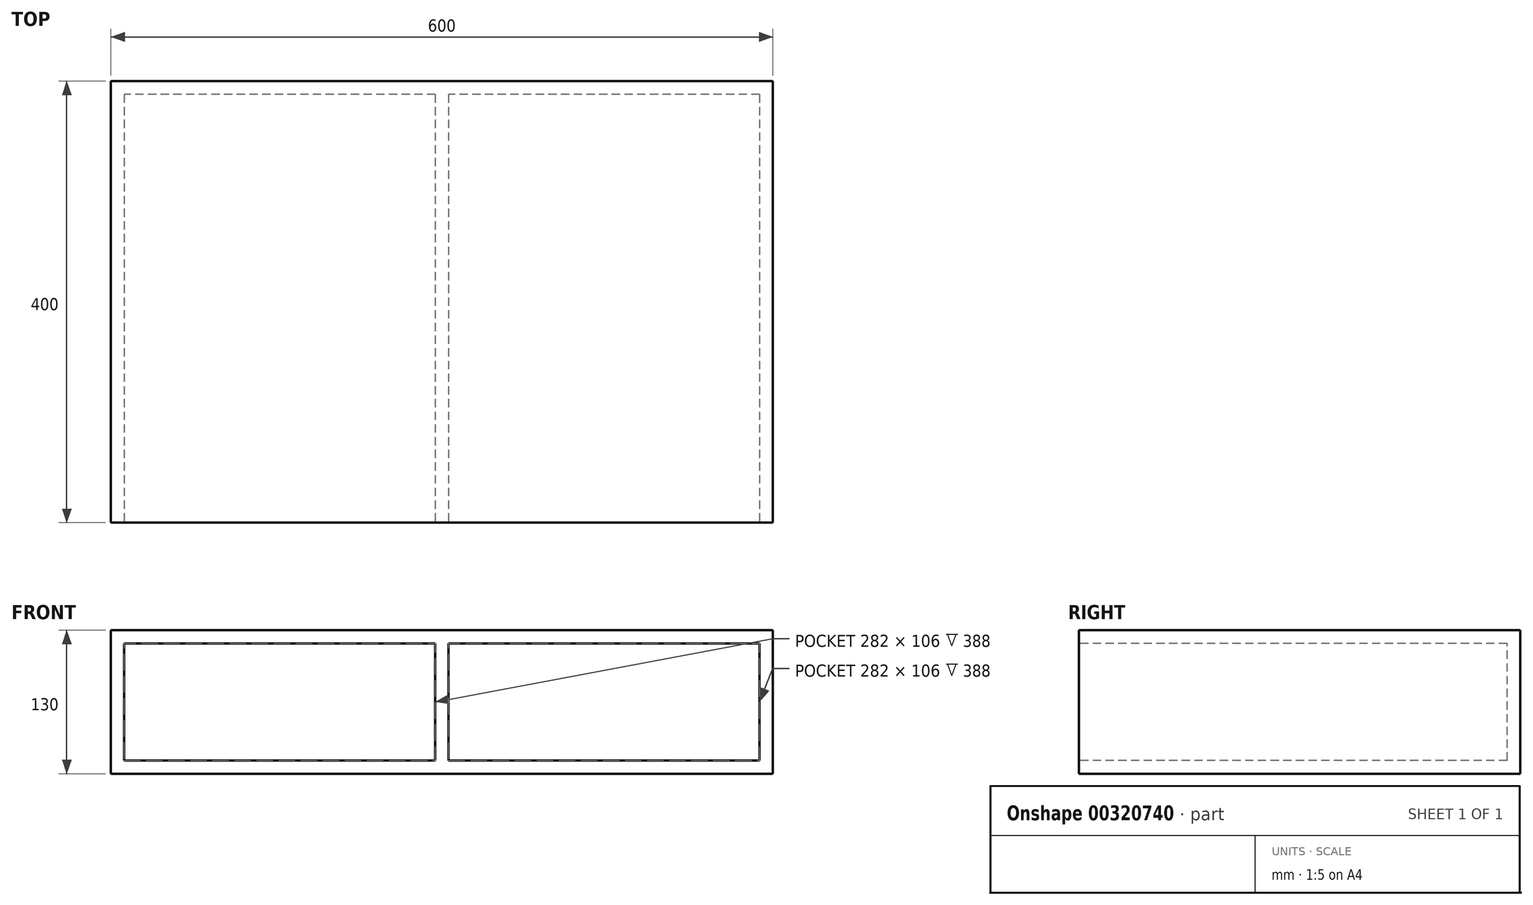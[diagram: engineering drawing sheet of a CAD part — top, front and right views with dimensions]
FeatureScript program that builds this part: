
annotation { "Feature Type Name" : "Feature", "Feature Type Description" : "" }
export const myFeature = defineFeature(function(context is Context, id is Id, definition is map)
    precondition{}
    {
        {
            var Q0;
            Q0=qCreatedBy(makeId("Front.planeOp"),FACE);
            var sketch = newSketch(context, id + "F0", { "sketchPlane" : qUnion([Q0])});
            skLineSegment(sketch, "E0.bottom", {"start": v(300, -65) * mm, "end": v(-300, -65) * mm});
            skLineSegment(sketch, "E0.top", {"start": v(300, 65) * mm, "end": v(-300, 65) * mm});
            skLineSegment(sketch, "E0.left", {"start": v(300, -65) * mm, "end": v(300, 65) * mm});
            skLineSegment(sketch, "E0.right", {"start": v(-300, -65) * mm, "end": v(-300, 65) * mm});
            skPoint(sketch, "E0.middle", {"position": v(0, 0) * mm});
            skSolve(sketch);
        }
        {
            var Q0;
            Q0=makeQuery(id+"F0.imprint","IMPRINT",FACE,{"disambiguationData":[TD([[makeQuery(id+"F0.imprint","IMPRINT",EDGE,{"derivedFrom":sQuery(id+"F0.wireOp",EDGE,"E0.bottom")}),-1.0]])]});
            extrude(context, id + "F1", {"entities" : qUnion([Q0]), "oppositeDirection" : true, "depth" : 400 * mm});
        }
        {
            var Q0;
            Q0=makeQuery(id+"F1.opExtrude","CAP_FACE",FACE,{"disambiguationData":[OSD([sQuery(id+"F0.wireOp",EDGE,"E0.bottom"),sQuery(id+"F0.wireOp",EDGE,"E0.top"),sQuery(id+"F0.wireOp",EDGE,"E0.left"),sQuery(id+"F0.wireOp",EDGE,"E0.right")])],"isStart":true});
            shell(context, id + "F2", {"entities" : qUnion([Q0]), "thickness" : 12 * mm});
        }
        {
            var Q0;
            Q0=makeQuery(id+"F1.opExtrude","CAP_FACE",FACE,{"disambiguationData":[OSD([sQuery(id+"F0.wireOp",EDGE,"E0.bottom"),sQuery(id+"F0.wireOp",EDGE,"E0.top"),sQuery(id+"F0.wireOp",EDGE,"E0.left"),sQuery(id+"F0.wireOp",EDGE,"E0.right")])],"isStart":true});
            var sketch = newSketch(context, id + "F3", { "sketchPlane" : qUnion([Q0])});
            skLineSegment(sketch, "E1.bottom", {"start": v(6, -62.5) * mm, "end": v(-6, -62.5) * mm});
            skLineSegment(sketch, "E1.top", {"start": v(6, 62.5) * mm, "end": v(-6, 62.5) * mm});
            skLineSegment(sketch, "E1.left", {"start": v(6, -62.5) * mm, "end": v(6, 62.5) * mm});
            skLineSegment(sketch, "E1.right", {"start": v(-6, -62.5) * mm, "end": v(-6, 62.5) * mm});
            skPoint(sketch, "E1.middle", {"position": v(0, 0) * mm});
            skSolve(sketch);
        }
        {
            var Q0;
            {var subQ0=sQuery(id+"F3.wireOp",EDGE,"E1.left");var subQ1=sQuery(id+"F0.wireOp",EDGE,"E0.bottom");var subQ2=makeQuery(id+"F2.opShell","OFFSET_EDGE",EDGE,{"disambiguationData":[OSD([subQ1]),TDD([makeQuery(id+"F1.opExtrude","CAP_EDGE",EDGE,{"disambiguationData":[OSD([subQ1])],"isStart":true})])]});var subQ3=makeQuery(id+"F3.imprint","INTERSECT",VERTEX,{"derivedFrom":[subQ2,subQ0]});Q0=makeQuery(id+"F3.imprint","IMPRINT",FACE,{"disambiguationData":[TD([[makeQuery(id+"F3.imprint","IMPRINT",EDGE,{"disambiguationData":[TD([[subQ3,-1.0]])],"derivedFrom":subQ0}),1.0]])]});}
            extrude(context, id + "F4", {"entities" : qUnion([Q0]), "operationType" : NewBodyOperationType.ADD, "oppositeDirection" : true, "depth" : 400 * mm});
        }
    });
